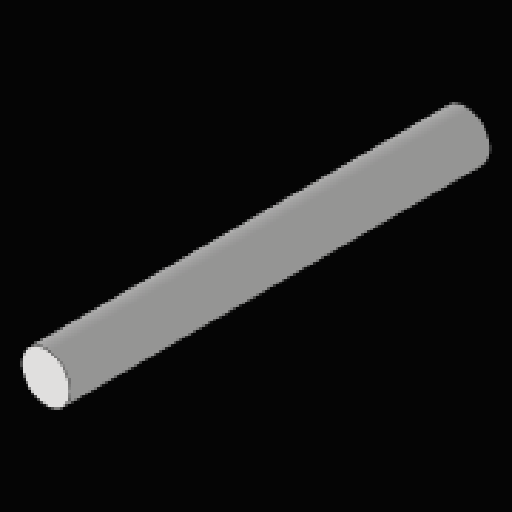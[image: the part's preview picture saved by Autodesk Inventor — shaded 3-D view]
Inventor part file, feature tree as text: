
AUTODESK INVENTOR PART (.ipt)
format: ipt  version: 2023.2 (Build 272271030, 271C)  size: 76,800 bytes
history: native  units: mm
features: extrude x1, sketch x1
ambient origin geometry x8: Origin, YZ Plane, XZ Plane, XY Plane, X Axis, Y Axis, Z Axis, Center Point
bodies: Solid1 (feature_tree)
feature tree (2):
  extrude  "Extrusion1"  Depth=51.3mm TaperAngle=0.0deg
  sketch  "Sketch1"  dims[d0=6.0mm d1=51.3mm d2=0.0mm]
